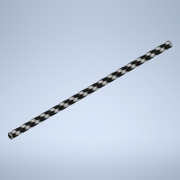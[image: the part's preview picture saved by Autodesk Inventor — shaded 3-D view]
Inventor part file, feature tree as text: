
AUTODESK INVENTOR PART (.ipt)
format: ipt  version: 2020 (Build 240168000, 168)  size: 102,912 bytes
history: native  units: in
note: dims shown in document units (in); Inventor stores cm internally (conversion verified against a paired STEP export)
features: extrude x1, sketch x1
ambient origin geometry x8: Origin, YZ Plane, XZ Plane, XY Plane, X Axis, Y Axis, Z Axis, Center Point
bodies: Solid1 (feature_tree)
feature tree (2):
  extrude  "Extrusion1"  Depth=2.4409in
  sketch  "Sketch1"  dims[d0=0.0787in d1=2.4409in d2=0.0in]
